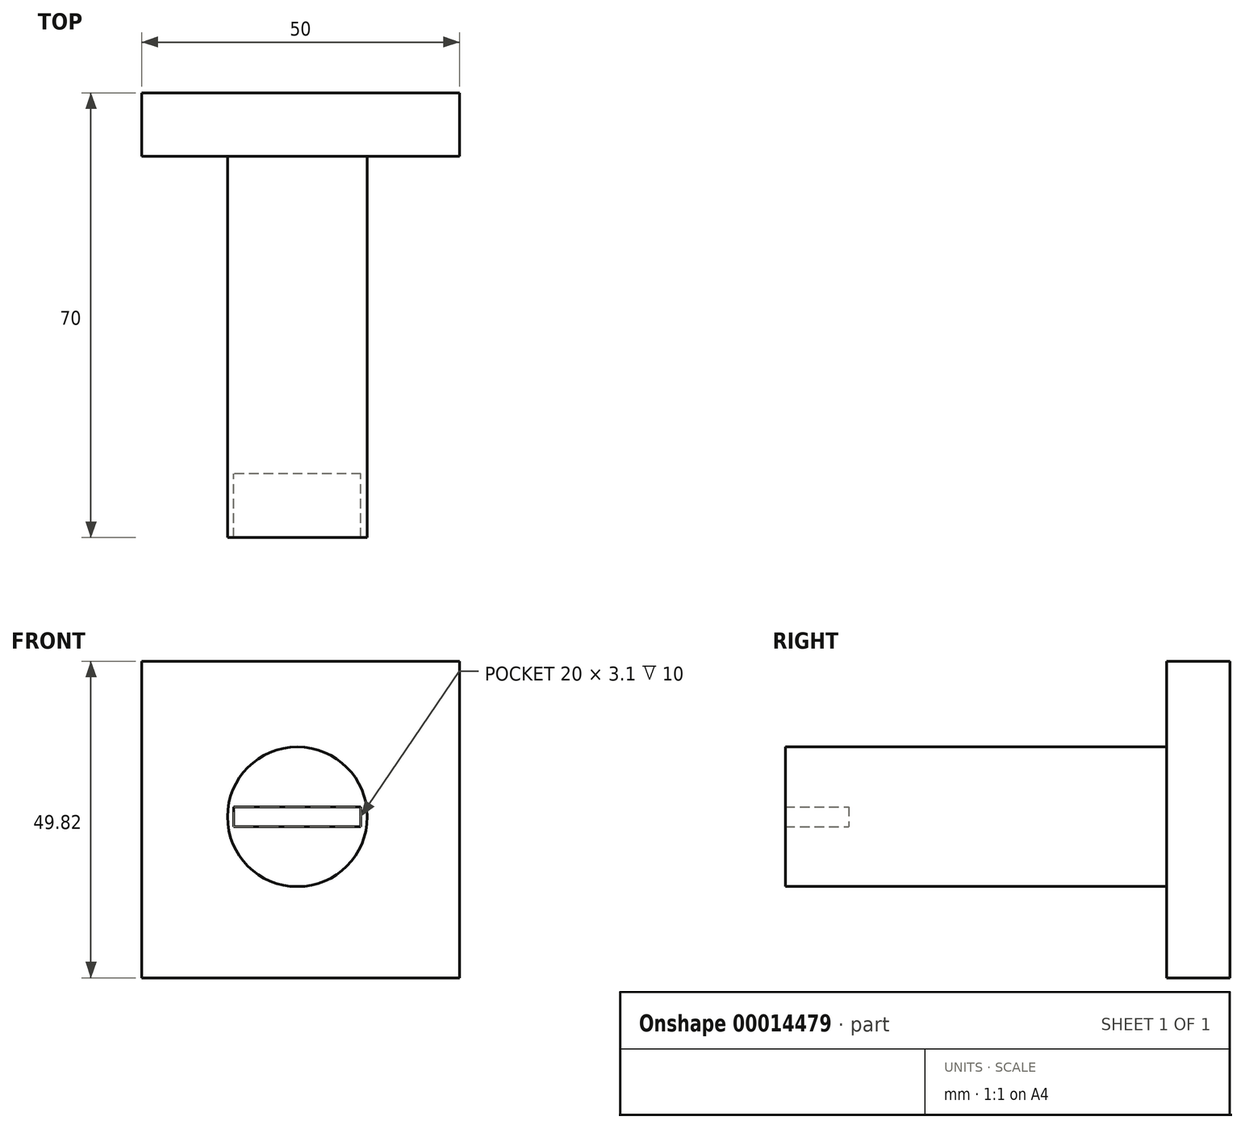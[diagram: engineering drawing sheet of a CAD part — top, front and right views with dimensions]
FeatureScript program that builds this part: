
annotation { "Feature Type Name" : "Feature", "Feature Type Description" : "" }
export const myFeature = defineFeature(function(context is Context, id is Id, definition is map)
    precondition{}
    {
        {
            var Q0;
            Q0=qCreatedBy(makeId("Front.planeOp"),FACE);
            var sketch = newSketch(context, id + "F0", { "sketchPlane" : qUnion([Q0])});
            skLineSegment(sketch, "E0.bottom", {"start": v(-24.49, 24.46) * mm, "end": v(25.51, 24.46) * mm});
            skLineSegment(sketch, "E0.top", {"start": v(-24.49, -25.36) * mm, "end": v(25.51, -25.36) * mm});
            skLineSegment(sketch, "E0.left", {"start": v(-24.49, 24.46) * mm, "end": v(-24.49, -25.36) * mm});
            skLineSegment(sketch, "E0.right", {"start": v(25.51, 24.46) * mm, "end": v(25.51, -25.36) * mm});
            skSolve(sketch);
        }
        {
            var Q0;
            Q0=makeQuery(id+"F0.imprint","IMPRINT",FACE,{"disambiguationData":[TD([[makeQuery(id+"F0.imprint","IMPRINT",EDGE,{"derivedFrom":sQuery(id+"F0.wireOp",EDGE,"E0.bottom")}),-1.0]])]});
            var Q1;
            Q1 = qSketchRegion(id + "F0", true);
            extrude(context, id + "F1", {"entities" : qUnion([Q0, Q1]), "depth" : 10 * mm});
        }
        {
            var Q0;
            Q0=makeQuery(id+"F1.opExtrude","CAP_FACE",FACE,{"disambiguationData":[OSD([sQuery(id+"F0.wireOp",EDGE,"E0.bottom"),sQuery(id+"F0.wireOp",EDGE,"E0.top"),sQuery(id+"F0.wireOp",EDGE,"E0.left"),sQuery(id+"F0.wireOp",EDGE,"E0.right")])],"isStart":false});
            var sketch = newSketch(context, id + "F2", { "sketchPlane" : qUnion([Q0])});
            skCircle(sketch, "E1", {"center": v(0, 0) * mm, "radius": 11 * mm});
            skSolve(sketch);
        }
        {
            var Q0;
            Q0=makeQuery(id+"F2.imprint","IMPRINT",FACE,{"disambiguationData":[TD([[makeQuery(id+"F2.imprint","IMPRINT",EDGE,{"derivedFrom":sQuery(id+"F2.wireOp",EDGE,"E1")}),1.0]])]});
            extrude(context, id + "F3", {"entities" : qUnion([Q0]), "operationType" : NewBodyOperationType.ADD, "depth" : 50 * mm});
        }
        {
            var Q0;
            Q0=makeQuery(id+"F3.opExtrude","CAP_FACE",FACE,{"disambiguationData":[OSD([sQuery(id+"F2.wireOp",EDGE,"E1")])],"isStart":false});
            var sketch = newSketch(context, id + "F4", { "sketchPlane" : qUnion([Q0])});
            skSolve(sketch);
        }
        {
            var Q0;
            Q0=makeQuery(id+"F4.imprint","IMPRINT",FACE,{"disambiguationData":[TD([[makeQuery(id+"F4.imprint","IMPRINT",EDGE,{"derivedFrom":makeQuery(id+"F3.opExtrude","CAP_EDGE",EDGE,{"disambiguationData":[OSD([sQuery(id+"F2.wireOp",EDGE,"E1")])],"isStart":false})}),1.0]])]});
            var sketch = newSketch(context, id + "F5", { "sketchPlane" : qUnion([Q0])});
            skCircle(sketch, "E2", {"center": v(0, 0) * mm, "radius": 11 * mm});
            skLineSegment(sketch, "E3.rect.bottom", {"start": v(10, 1.55) * mm, "end": v(-10, 1.55) * mm});
            skLineSegment(sketch, "E3.rect.top", {"start": v(10, -1.55) * mm, "end": v(-10, -1.55) * mm});
            skLineSegment(sketch, "E3.rect.left", {"start": v(10, 1.55) * mm, "end": v(10, -1.55) * mm});
            skLineSegment(sketch, "E3.rect.right", {"start": v(-10, 1.55) * mm, "end": v(-10, -1.55) * mm});
            skSolve(sketch);
        }
        {
            var Q0;
            Q0=makeQuery(id+"F5.imprint","IMPRINT",FACE,{"disambiguationData":[TD([[makeQuery(id+"F5.imprint","IMPRINT",EDGE,{"derivedFrom":sQuery(id+"F5.wireOp",EDGE,"E2")}),1.0]])]});
            var sketch = newSketch(context, id + "F6", { "sketchPlane" : qUnion([Q0])});
            skSolve(sketch);
        }
        {
            var Q0;
            Q0=makeQuery(id+"F6.imprint","IMPRINT",FACE,{"disambiguationData":[TD([[makeQuery(id+"F6.imprint","IMPRINT",EDGE,{"derivedFrom":makeQuery(id+"F5.imprint","IMPRINT",EDGE,{"derivedFrom":sQuery(id+"F5.wireOp",EDGE,"E2")})}),1.0]])]});
            extrude(context, id + "F7", {"entities" : qUnion([Q0]), "operationType" : NewBodyOperationType.ADD, "depth" : 10 * mm});
        }
    });
